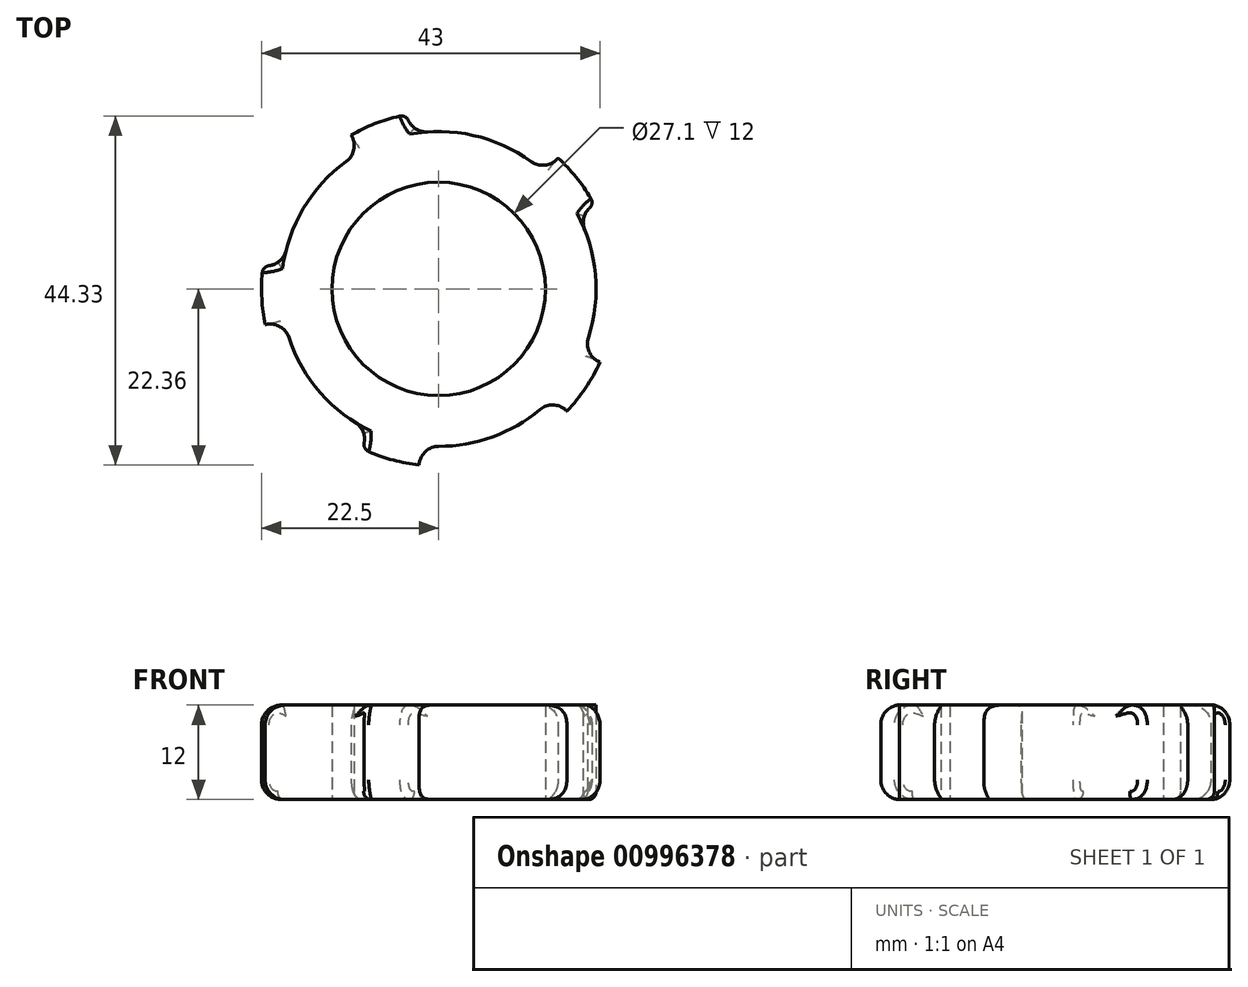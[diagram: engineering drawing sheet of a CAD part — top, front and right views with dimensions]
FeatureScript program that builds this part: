
annotation { "Feature Type Name" : "Feature", "Feature Type Description" : "" }
export const myFeature = defineFeature(function(context is Context, id is Id, definition is map)
    precondition{}
    {
        {
            var Q0;
            Q0=qCreatedBy(makeId("Top.planeOp"),FACE);
            var sketch = newSketch(context, id + "F0", { "sketchPlane" : qUnion([Q0])});
            skCircle(sketch, "E0", {"center": v(0, 0) * mm, "radius": 13.55 * mm});
            skCircle(sketch, "E1", {"center": v(0, 0) * mm, "radius": 20 * mm});
            skCircle(sketch, "E2", {"center": v(0, 0) * mm, "radius": 22.5 * mm});
            skSolve(sketch);
        }
        {
            var Q0;
            Q0=makeQuery(id+"F0.imprint","IMPRINT",FACE,{"disambiguationData":[TD([[makeQuery(id+"F0.imprint","IMPRINT",EDGE,{"derivedFrom":sQuery(id+"F0.wireOp",EDGE,"r8lv5OWj-RZf0-Jlgv-olLd-SWOEOWRyUNaY")}),-1.0]])]});
            var Q1;
            Q1=makeQuery(id+"F0.imprint","IMPRINT",FACE,{"disambiguationData":[TD([[makeQuery(id+"F0.imprint","IMPRINT",EDGE,{"derivedFrom":sQuery(id+"F0.wireOp",EDGE,"E0")}),-1.0]])]});
            extrude(context, id + "F1", {"entities" : qUnion([Q0, Q1]), "depth" : 15 * mm, "offsetDistance" : 25 * mm});
        }
        {
            var Q0;
            Q0=makeQuery(id+"F0.imprint","IMPRINT",FACE,{"disambiguationData":[TD([[makeQuery(id+"F0.imprint","IMPRINT",EDGE,{"derivedFrom":sQuery(id+"F0.wireOp",EDGE,"E1")}),-1.0]])]});
            extrude(context, id + "F2", {"entities" : qUnion([Q0]), "operationType" : NewBodyOperationType.ADD, "depth" : 12 * mm, "offsetDistance" : 25 * mm});
        }
        {
            var Q0;
            Q0=makeQuery(id+"F0.imprint","IMPRINT",FACE,{"disambiguationData":[TD([[makeQuery(id+"F0.imprint","IMPRINT",EDGE,{"derivedFrom":sQuery(id+"F0.wireOp",EDGE,"E1")}),-1.0]])]});
            var sketch = newSketch(context, id + "F3", { "sketchPlane" : qUnion([Q0])});
            skCircle(sketch, "E3", {"center": v(0, -22.5) * mm, "radius": 2.5 * mm});
            skLineSegment(sketch, "E4", {"start": v(0, 0) * mm, "end": v(14.46, -17.24) * mm, "construction": true});
            skCircle(sketch, "E5", {"center": v(14.46, -17.24) * mm, "radius": 2.5 * mm});
            skArc(sketch, "E6", {"start": v(0, -20) * mm, "mid": v(6.84, -18.8) * mm, "end": v(12.86, -15.32) * mm});
            skArc(sketch, "E7", {"start": v(0, -25) * mm, "mid": v(8.47, -23.4) * mm, "end": v(16.01, -19.2) * mm});
            skSolve(sketch);
        }
        {
            var Q0;
            Q0=qCreatedBy(makeId("Right.planeOp"),FACE);
            var sketch = newSketch(context, id + "F4", { "sketchPlane" : qUnion([Q0])});
            skLineSegment(sketch, "E8", {"start": v(0, 0) * mm, "end": v(0, 36.07) * mm, "construction": true});
            skSolve(sketch);
        }
        {
            var Q0;
            {var subQ0=sQuery(id+"F3.wireOp",EDGE,"E7");var subQ1=sQuery(id+"F3.wireOp",EDGE,"E3");var subQ2=makeQuery(id+"F3.imprint","INTERSECT",VERTEX,{"disambiguationData":[OD(0.0)],"derivedFrom":[subQ1,subQ0]});Q0=makeQuery(id+"F3.imprint","IMPRINT",FACE,{"disambiguationData":[TD([[makeQuery(id+"F3.imprint","IMPRINT",EDGE,{"disambiguationData":[TD([[subQ2,1.0]])],"derivedFrom":subQ1}),1.0]])]});}
            var Q1;
            {var subQ0=sQuery(id+"F3.wireOp",EDGE,"E3");var subQ2=makeQuery(id+"F0.imprint","IMPRINT",EDGE,{"derivedFrom":sQuery(id+"F0.wireOp",EDGE,"E2")});var subQ4=makeQuery(id+"F3.imprint","INTERSECT",VERTEX,{"disambiguationData":[OD(0.0)],"derivedFrom":[subQ2,subQ0]});Q1=makeQuery(id+"F3.imprint","IMPRINT",FACE,{"disambiguationData":[TD([[makeQuery(id+"F3.imprint","IMPRINT",EDGE,{"disambiguationData":[TD([[subQ4,-1.0]])],"derivedFrom":subQ2}),1.0]])]});}
            var Q2;
            {var subQ0=sQuery(id+"F3.wireOp",EDGE,"E6");Q2=makeQuery(id+"F3.imprint","IMPRINT",FACE,{"disambiguationData":[TD([[makeQuery(id+"F3.imprint","IMPRINT",EDGE,{"derivedFrom":subQ0}),-1.0]])]});}
            var Q3;
            {var subQ0=sQuery(id+"F3.wireOp",EDGE,"E5");var subQ2=makeQuery(id+"F0.imprint","IMPRINT",EDGE,{"derivedFrom":sQuery(id+"F0.wireOp",EDGE,"E2")});var subQ3=makeQuery(id+"F3.imprint","INTERSECT",VERTEX,{"disambiguationData":[OD(0.0)],"derivedFrom":[subQ2,subQ0]});Q3=makeQuery(id+"F3.imprint","IMPRINT",FACE,{"disambiguationData":[TD([[makeQuery(id+"F3.imprint","IMPRINT",EDGE,{"disambiguationData":[TD([[subQ3,1.0]])],"derivedFrom":subQ2}),1.0]])]});}
            var Q4;
            {var subQ0=sQuery(id+"F3.wireOp",EDGE,"E5");var subQ1=makeQuery(id+"F3.imprint","INTERSECT",VERTEX,{"derivedFrom":[subQ0,sQuery(id+"F3.wireOp",EDGE,"E7")]});Q4=makeQuery(id+"F3.imprint","IMPRINT",FACE,{"disambiguationData":[TD([[makeQuery(id+"F3.imprint","IMPRINT",EDGE,{"disambiguationData":[TD([[subQ1,1.0]])],"derivedFrom":subQ0}),1.0]])]});}
            var Q5;
            {var subQ0=sQuery(id+"F3.wireOp",EDGE,"E7");var subQ1=sQuery(id+"F3.wireOp",EDGE,"E3");var subQ2=makeQuery(id+"F3.imprint","INTERSECT",VERTEX,{"disambiguationData":[OD(1.0)],"derivedFrom":[subQ1,subQ0]});Q5=makeQuery(id+"F3.imprint","IMPRINT",FACE,{"disambiguationData":[TD([[makeQuery(id+"F3.imprint","IMPRINT",EDGE,{"disambiguationData":[TD([[subQ2,-1.0]])],"derivedFrom":subQ1}),-1.0]])]});}
            extrude(context, id + "F5", {"entities" : qUnion([Q0, Q1, Q2, Q3, Q4, Q5]), "operationType" : NewBodyOperationType.REMOVE, "depth" : 25 * mm, "offsetDistance" : 25 * mm});
        }
        {
            var Q0;
            Q0=makeQuery(id+"F1.opExtrude","SWEPT_BODY",BODY,{"disambiguationData":[OSD([sQuery(id+"F0.wireOp",EDGE,"r8lv5OWj-RZf0-Jlgv-olLd-SWOEOWRyUNaY"),sQuery(id+"F0.wireOp",EDGE,"E1")])]});
            var Q1;
            Q1=sQuery(id+"F4.wireOp",EDGE,"E8");
            circularPattern(context, id + "F6", {"entities" : qUnion([Q0]), "axis" : qUnion([Q1]), "angle" : 360 * degree, "instanceCount" : 5, "equalSpace" : true});
        }
        {
            var Q0;
            Q0=makeQuery(id+"F6.opPattern","COPY",BODY,{"derivedFrom":makeQuery(id+"F1.opExtrude","SWEPT_BODY",BODY,{"disambiguationData":[OSD([sQuery(id+"F0.wireOp",EDGE,"r8lv5OWj-RZf0-Jlgv-olLd-SWOEOWRyUNaY"),sQuery(id+"F0.wireOp",EDGE,"E1")])]}),"instanceName":"4"});
            var Q1;
            Q1=makeQuery(id+"F6.opPattern","COPY",BODY,{"derivedFrom":makeQuery(id+"F1.opExtrude","SWEPT_BODY",BODY,{"disambiguationData":[OSD([sQuery(id+"F0.wireOp",EDGE,"r8lv5OWj-RZf0-Jlgv-olLd-SWOEOWRyUNaY"),sQuery(id+"F0.wireOp",EDGE,"E1")])]}),"instanceName":"3"});
            var Q2;
            Q2=makeQuery(id+"F6.opPattern","COPY",BODY,{"derivedFrom":makeQuery(id+"F1.opExtrude","SWEPT_BODY",BODY,{"disambiguationData":[OSD([sQuery(id+"F0.wireOp",EDGE,"r8lv5OWj-RZf0-Jlgv-olLd-SWOEOWRyUNaY"),sQuery(id+"F0.wireOp",EDGE,"E1")])]}),"instanceName":"2"});
            var Q3;
            Q3=makeQuery(id+"F6.opPattern","COPY",BODY,{"derivedFrom":makeQuery(id+"F1.opExtrude","SWEPT_BODY",BODY,{"disambiguationData":[OSD([sQuery(id+"F0.wireOp",EDGE,"r8lv5OWj-RZf0-Jlgv-olLd-SWOEOWRyUNaY"),sQuery(id+"F0.wireOp",EDGE,"E1")])]}),"instanceName":"1"});
            var Q4;
            Q4=makeQuery(id+"F1.opExtrude","SWEPT_BODY",BODY,{"disambiguationData":[OSD([sQuery(id+"F0.wireOp",EDGE,"r8lv5OWj-RZf0-Jlgv-olLd-SWOEOWRyUNaY"),sQuery(id+"F0.wireOp",EDGE,"E1")])]});
            booleanBodies(context, id + "F7", {"operationType" : BooleanOperationType.INTERSECTION, "tools" : qUnion([Q0, Q1, Q2, Q3, Q4])});
        }
        {
            var Q0;
            {var subQ0=sQuery(id+"F0.wireOp",EDGE,"E2");Q0=makeQuery(id+"F7.opBoolean","SPLIT",EDGE,{"disambiguationData":[TD([makeQuery(id+"F5.boolean.opBoolean","COPY",FACE,{"derivedFrom":makeQuery(id+"F5.opExtrude","SWEPT_FACE",FACE,{"disambiguationData":[OSD([sQuery(id+"F3.wireOp",EDGE,"E3")])]})})])],"derivedFrom":makeQuery(id+"F6.opPattern","COPY",EDGE,{"derivedFrom":makeQuery(id+"F2.opExtrude","CAP_EDGE",EDGE,{"disambiguationData":[OSD([subQ0])],"isStart":false}),"instanceName":"4"})});}
            var Q1;
            {var subQ0=sQuery(id+"F0.wireOp",EDGE,"E2");Q1=makeQuery(id+"F7.opBoolean","SPLIT",EDGE,{"disambiguationData":[TD([makeQuery(id+"F6.opPattern","COPY",FACE,{"derivedFrom":makeQuery(id+"F5.boolean.opBoolean","COPY",FACE,{"derivedFrom":makeQuery(id+"F5.opExtrude","SWEPT_FACE",FACE,{"disambiguationData":[OSD([sQuery(id+"F3.wireOp",EDGE,"E5")])]})}),"instanceName":"3"})])],"derivedFrom":makeQuery(id+"F6.opPattern","COPY",EDGE,{"derivedFrom":makeQuery(id+"F2.opExtrude","CAP_EDGE",EDGE,{"disambiguationData":[OSD([subQ0])],"isStart":false}),"instanceName":"4"})});}
            var Q2;
            {var subQ0=sQuery(id+"F0.wireOp",EDGE,"E2");Q2=makeQuery(id+"F7.opBoolean","SPLIT",EDGE,{"disambiguationData":[TD([makeQuery(id+"F6.opPattern","COPY",FACE,{"derivedFrom":makeQuery(id+"F5.boolean.opBoolean","COPY",FACE,{"derivedFrom":makeQuery(id+"F5.opExtrude","SWEPT_FACE",FACE,{"disambiguationData":[OSD([sQuery(id+"F3.wireOp",EDGE,"E5")])]})}),"instanceName":"2"})])],"derivedFrom":makeQuery(id+"F6.opPattern","COPY",EDGE,{"derivedFrom":makeQuery(id+"F2.opExtrude","CAP_EDGE",EDGE,{"disambiguationData":[OSD([subQ0])],"isStart":false}),"instanceName":"4"})});}
            var Q3;
            {var subQ0=sQuery(id+"F0.wireOp",EDGE,"E2");Q3=makeQuery(id+"F7.opBoolean","SPLIT",EDGE,{"disambiguationData":[TD([makeQuery(id+"F6.opPattern","COPY",FACE,{"derivedFrom":makeQuery(id+"F5.boolean.opBoolean","COPY",FACE,{"derivedFrom":makeQuery(id+"F5.opExtrude","SWEPT_FACE",FACE,{"disambiguationData":[OSD([sQuery(id+"F3.wireOp",EDGE,"E5")])]})}),"instanceName":"1"})])],"derivedFrom":makeQuery(id+"F6.opPattern","COPY",EDGE,{"derivedFrom":makeQuery(id+"F2.opExtrude","CAP_EDGE",EDGE,{"disambiguationData":[OSD([subQ0])],"isStart":false}),"instanceName":"4"})});}
            var Q4;
            {var subQ0=sQuery(id+"F0.wireOp",EDGE,"E2");Q4=makeQuery(id+"F7.opBoolean","SPLIT",EDGE,{"disambiguationData":[TD([makeQuery(id+"F5.boolean.opBoolean","COPY",FACE,{"derivedFrom":makeQuery(id+"F5.opExtrude","SWEPT_FACE",FACE,{"disambiguationData":[OSD([sQuery(id+"F3.wireOp",EDGE,"E5")])]})})])],"derivedFrom":makeQuery(id+"F6.opPattern","COPY",EDGE,{"derivedFrom":makeQuery(id+"F2.opExtrude","CAP_EDGE",EDGE,{"disambiguationData":[OSD([subQ0])],"isStart":false}),"instanceName":"4"})});}
            var Q5;
            {var subQ0=sQuery(id+"F0.wireOp",EDGE,"E2");Q5=makeQuery(id+"F7.opBoolean","SPLIT",EDGE,{"disambiguationData":[TD([makeQuery(id+"F5.boolean.opBoolean","COPY",FACE,{"derivedFrom":makeQuery(id+"F5.opExtrude","SWEPT_FACE",FACE,{"disambiguationData":[OSD([sQuery(id+"F3.wireOp",EDGE,"E3")])]})})])],"derivedFrom":makeQuery(id+"F6.opPattern","COPY",EDGE,{"derivedFrom":makeQuery(id+"F2.opExtrude","CAP_EDGE",EDGE,{"disambiguationData":[OSD([subQ0])],"isStart":true}),"instanceName":"4"})});}
            var Q6;
            {var subQ0=sQuery(id+"F0.wireOp",EDGE,"E2");Q6=makeQuery(id+"F7.opBoolean","SPLIT",EDGE,{"disambiguationData":[TD([makeQuery(id+"F6.opPattern","COPY",FACE,{"derivedFrom":makeQuery(id+"F5.boolean.opBoolean","COPY",FACE,{"derivedFrom":makeQuery(id+"F5.opExtrude","SWEPT_FACE",FACE,{"disambiguationData":[OSD([sQuery(id+"F3.wireOp",EDGE,"E5")])]})}),"instanceName":"3"})])],"derivedFrom":makeQuery(id+"F6.opPattern","COPY",EDGE,{"derivedFrom":makeQuery(id+"F2.opExtrude","CAP_EDGE",EDGE,{"disambiguationData":[OSD([subQ0])],"isStart":true}),"instanceName":"4"})});}
            var Q7;
            {var subQ0=sQuery(id+"F0.wireOp",EDGE,"E2");Q7=makeQuery(id+"F7.opBoolean","SPLIT",EDGE,{"disambiguationData":[TD([makeQuery(id+"F5.boolean.opBoolean","COPY",FACE,{"derivedFrom":makeQuery(id+"F5.opExtrude","SWEPT_FACE",FACE,{"disambiguationData":[OSD([sQuery(id+"F3.wireOp",EDGE,"E5")])]})})])],"derivedFrom":makeQuery(id+"F6.opPattern","COPY",EDGE,{"derivedFrom":makeQuery(id+"F2.opExtrude","CAP_EDGE",EDGE,{"disambiguationData":[OSD([subQ0])],"isStart":true}),"instanceName":"4"})});}
            var Q8;
            {var subQ0=sQuery(id+"F0.wireOp",EDGE,"E2");Q8=makeQuery(id+"F7.opBoolean","SPLIT",EDGE,{"disambiguationData":[TD([makeQuery(id+"F6.opPattern","COPY",FACE,{"derivedFrom":makeQuery(id+"F5.boolean.opBoolean","COPY",FACE,{"derivedFrom":makeQuery(id+"F5.opExtrude","SWEPT_FACE",FACE,{"disambiguationData":[OSD([sQuery(id+"F3.wireOp",EDGE,"E5")])]})}),"instanceName":"1"})])],"derivedFrom":makeQuery(id+"F6.opPattern","COPY",EDGE,{"derivedFrom":makeQuery(id+"F2.opExtrude","CAP_EDGE",EDGE,{"disambiguationData":[OSD([subQ0])],"isStart":true}),"instanceName":"4"})});}
            var Q9;
            {var subQ0=sQuery(id+"F0.wireOp",EDGE,"E2");Q9=makeQuery(id+"F7.opBoolean","SPLIT",EDGE,{"disambiguationData":[TD([makeQuery(id+"F6.opPattern","COPY",FACE,{"derivedFrom":makeQuery(id+"F5.boolean.opBoolean","COPY",FACE,{"derivedFrom":makeQuery(id+"F5.opExtrude","SWEPT_FACE",FACE,{"disambiguationData":[OSD([sQuery(id+"F3.wireOp",EDGE,"E5")])]})}),"instanceName":"2"})])],"derivedFrom":makeQuery(id+"F6.opPattern","COPY",EDGE,{"derivedFrom":makeQuery(id+"F2.opExtrude","CAP_EDGE",EDGE,{"disambiguationData":[OSD([subQ0])],"isStart":true}),"instanceName":"4"})});}
            fillet(context, id + "F8", {"entities" : qUnion([Q0, Q1, Q2, Q3, Q4, Q5, Q6, Q7, Q8, Q9]), "radius" : 2.5 * mm, "tangentPropagation" : true, "allowEdgeOverflow" : false});
        }
        {
            var Q0;
            Q0=makeQuery(id+"F5.boolean.opBoolean","INTERSECT",EDGE,{"derivedFrom":[makeQuery(id+"F2.opExtrude","SWEPT_FACE",FACE,{"disambiguationData":[OSD([sQuery(id+"F0.wireOp",EDGE,"E2")])]}),makeQuery(id+"F5.opExtrude","SWEPT_FACE",FACE,{"disambiguationData":[OSD([sQuery(id+"F3.wireOp",EDGE,"E5")])]})]});
            var Q1;
            Q1=makeQuery(id+"F6.opPattern","COPY",EDGE,{"derivedFrom":makeQuery(id+"F5.boolean.opBoolean","INTERSECT",EDGE,{"derivedFrom":[makeQuery(id+"F2.opExtrude","SWEPT_FACE",FACE,{"disambiguationData":[OSD([sQuery(id+"F0.wireOp",EDGE,"E2")])]}),makeQuery(id+"F5.opExtrude","SWEPT_FACE",FACE,{"disambiguationData":[OSD([sQuery(id+"F3.wireOp",EDGE,"E5")])]})]}),"instanceName":"4"});
            var Q2;
            Q2=makeQuery(id+"F6.opPattern","COPY",EDGE,{"derivedFrom":makeQuery(id+"F5.boolean.opBoolean","INTERSECT",EDGE,{"derivedFrom":[makeQuery(id+"F2.opExtrude","SWEPT_FACE",FACE,{"disambiguationData":[OSD([sQuery(id+"F0.wireOp",EDGE,"E2")])]}),makeQuery(id+"F5.opExtrude","SWEPT_FACE",FACE,{"disambiguationData":[OSD([sQuery(id+"F3.wireOp",EDGE,"E5")])]})]}),"instanceName":"3"});
            var Q3;
            Q3=makeQuery(id+"F6.opPattern","COPY",EDGE,{"derivedFrom":makeQuery(id+"F5.boolean.opBoolean","INTERSECT",EDGE,{"derivedFrom":[makeQuery(id+"F2.opExtrude","SWEPT_FACE",FACE,{"disambiguationData":[OSD([sQuery(id+"F0.wireOp",EDGE,"E2")])]}),makeQuery(id+"F5.opExtrude","SWEPT_FACE",FACE,{"disambiguationData":[OSD([sQuery(id+"F3.wireOp",EDGE,"E5")])]})]}),"instanceName":"2"});
            var Q4;
            Q4=makeQuery(id+"F6.opPattern","COPY",EDGE,{"derivedFrom":makeQuery(id+"F5.boolean.opBoolean","INTERSECT",EDGE,{"derivedFrom":[makeQuery(id+"F2.opExtrude","SWEPT_FACE",FACE,{"disambiguationData":[OSD([sQuery(id+"F0.wireOp",EDGE,"E2")])]}),makeQuery(id+"F5.opExtrude","SWEPT_FACE",FACE,{"disambiguationData":[OSD([sQuery(id+"F3.wireOp",EDGE,"E5")])]})]}),"instanceName":"1"});
            fillet(context, id + "F9", {"entities" : qUnion([Q0, Q1, Q2, Q3, Q4]), "radius" : 1 * mm, "tangentPropagation" : true, "allowEdgeOverflow" : false});
        }
        {
            var Q0;
            Q0=makeQuery(id+"F6.opPattern","COPY",FACE,{"derivedFrom":makeQuery(id+"F1.opExtrude","CAP_FACE",FACE,{"disambiguationData":[OSD([sQuery(id+"F0.wireOp",EDGE,"E0"),sQuery(id+"F0.wireOp",EDGE,"E1")])],"isStart":false}),"instanceName":"4"});
            extrude(context, id + "F10", {"entities" : qUnion([Q0]), "operationType" : NewBodyOperationType.REMOVE, "oppositeDirection" : true, "depth" : 3 * mm, "offsetDistance" : 25 * mm});
        }
    });
